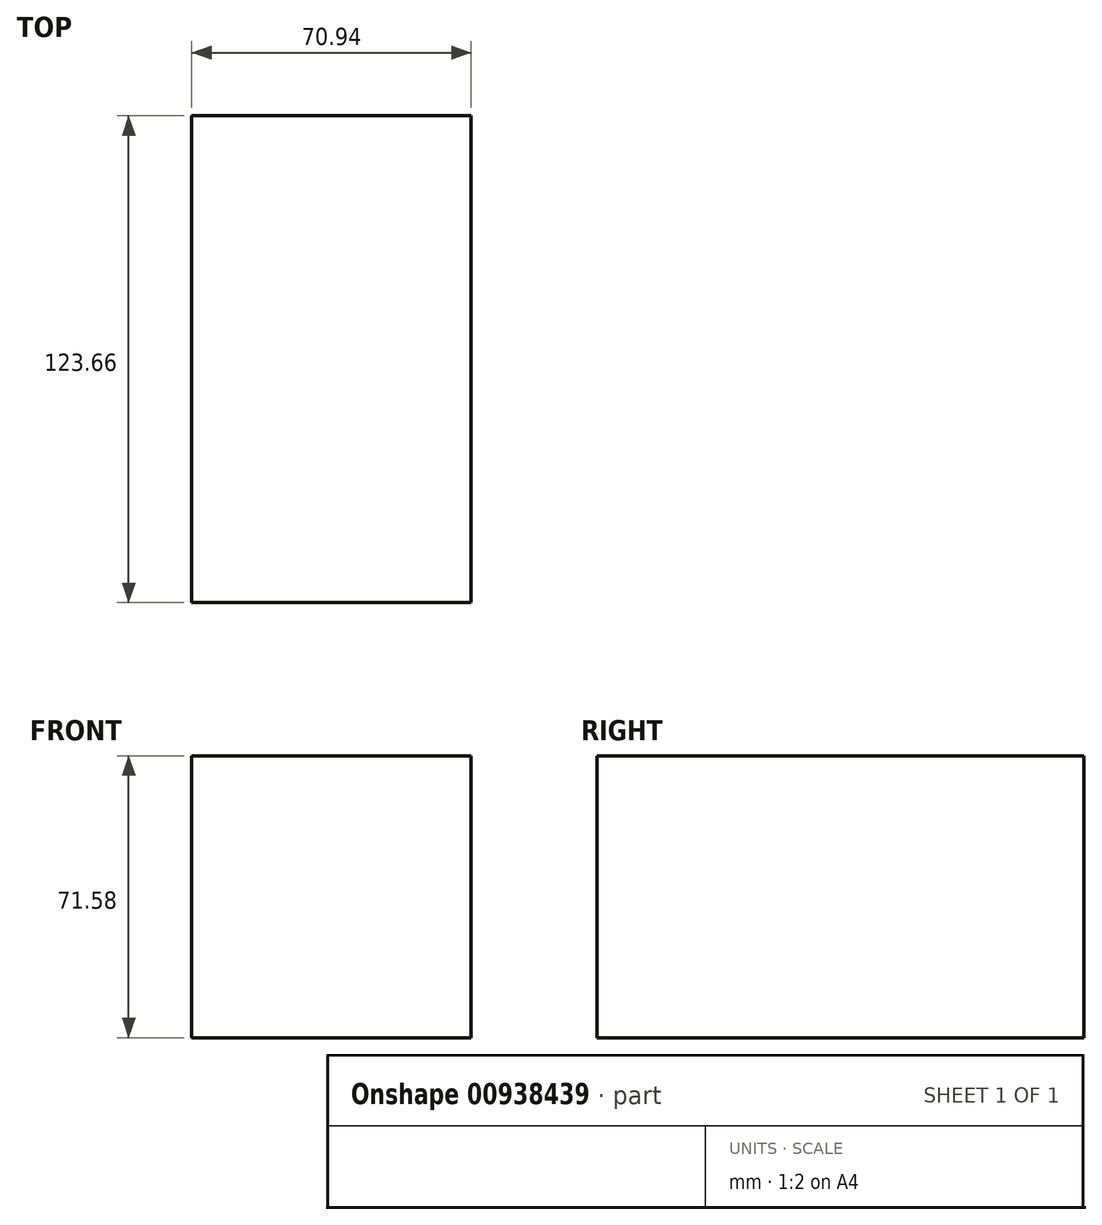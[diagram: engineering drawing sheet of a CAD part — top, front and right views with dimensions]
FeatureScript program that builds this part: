
annotation { "Feature Type Name" : "Feature", "Feature Type Description" : "" }
export const myFeature = defineFeature(function(context is Context, id is Id, definition is map)
    precondition{}
    {
        {
            var Q0;
            Q0=qCreatedBy(makeId("Front.planeOp"),FACE);
            var sketch = newSketch(context, id + "F0", { "sketchPlane" : qUnion([Q0])});
            skLineSegment(sketch, "E0.bottom", {"start": v(16.62, 42.62) * mm, "end": v(-54.32, 42.62) * mm});
            skLineSegment(sketch, "E0.top", {"start": v(16.62, -28.96) * mm, "end": v(-54.32, -28.96) * mm});
            skLineSegment(sketch, "E0.left", {"start": v(16.62, 42.62) * mm, "end": v(16.62, -28.96) * mm});
            skLineSegment(sketch, "E0.right", {"start": v(-54.32, 42.62) * mm, "end": v(-54.32, -28.96) * mm});
            skSolve(sketch);
        }
        {
            var Q0;
            Q0 = qSketchRegion(id + "F0", true);
            extrude(context, id + "F1", {"entities" : qUnion([Q0]), "depth" : 123.66 * mm, "offsetDistance" : 25.4 * mm});
        }
    });
